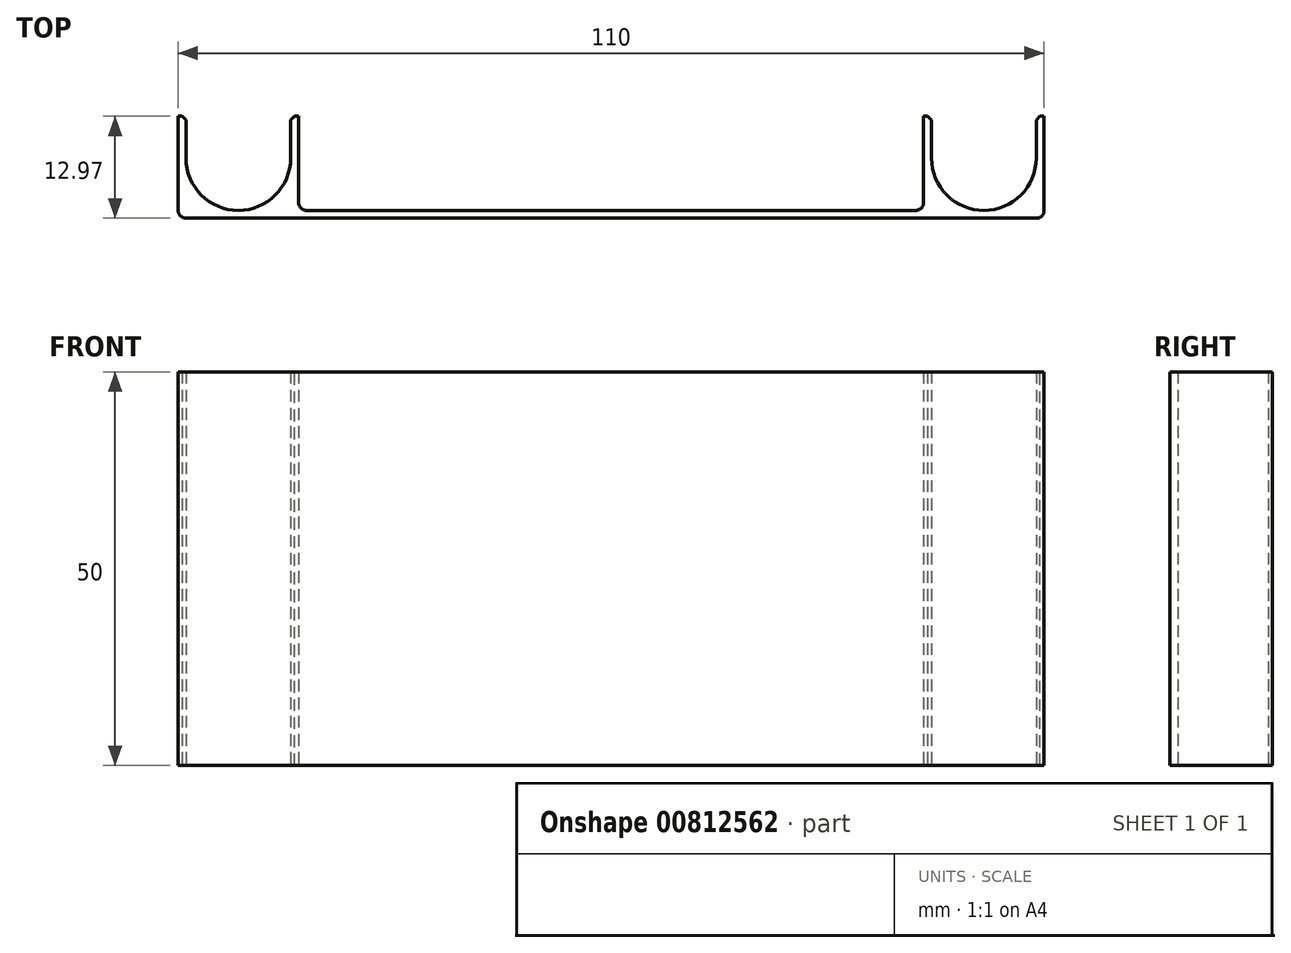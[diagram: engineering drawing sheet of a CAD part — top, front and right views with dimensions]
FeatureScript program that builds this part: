
annotation { "Feature Type Name" : "Feature", "Feature Type Description" : "" }
export const myFeature = defineFeature(function(context is Context, id is Id, definition is map)
    precondition{}
    {
        {
            assignVariable(context, id + "F0", {"name" : "length", "anyValue" : 50});
        }
        {
            var Q0;
            Q0=qCreatedBy(makeId("Top.planeOp"),FACE);
            var sketch = newSketch(context, id + "F1", { "sketchPlane" : qUnion([Q0])});
            skPoint(sketch, "E0.middle", {"position": v(0, 0) * mm});
            skLineSegment(sketch, "E1", {"start": v(-39.7, 1) * mm, "end": v(0, 1) * mm});
            skLineSegment(sketch, "E2", {"start": v(-55, 0) * mm, "end": v(0, 0) * mm});
            skLineSegment(sketch, "E3", {"start": v(0, 1) * mm, "end": v(0, 0) * mm, "construction": true});
            skLineSegment(sketch, "E4.MirrorCS", {"start": v(39.7, 1) * mm, "end": v(0, 1) * mm});
            skLineSegment(sketch, "E5.MirrorCS", {"start": v(55, 0) * mm, "end": v(0, 0) * mm});
            skLineSegment(sketch, "E6", {"start": v(-55, 0) * mm, "end": v(-55, 12.97) * mm});
            skLineSegment(sketch, "E7", {"start": v(-55, 12.97) * mm, "end": v(-54, 12.97) * mm});
            skLineSegment(sketch, "E8", {"start": v(-54, 12.97) * mm, "end": v(-54, 7.65) * mm});
            skLineSegment(sketch, "E9", {"start": v(-40.7, 7.65) * mm, "end": v(-40.7, 12.97) * mm});
            skLineSegment(sketch, "E10", {"start": v(-40.7, 12.97) * mm, "end": v(-39.7, 12.97) * mm});
            skLineSegment(sketch, "E11", {"start": v(-39.7, 12.97) * mm, "end": v(-39.7, 1) * mm});
            skLineSegment(sketch, "E12.MirrorCS", {"start": v(39.7, 12.97) * mm, "end": v(39.7, 1) * mm});
            skLineSegment(sketch, "E13.MirrorCS", {"start": v(40.7, 7.65) * mm, "end": v(40.7, 12.97) * mm});
            skLineSegment(sketch, "E14.MirrorCS", {"start": v(54, 12.97) * mm, "end": v(54, 7.65) * mm});
            skLineSegment(sketch, "E15.MirrorCS", {"start": v(55, 0) * mm, "end": v(55, 12.97) * mm});
            skLineSegment(sketch, "E16.MirrorCS", {"start": v(40.7, 12.97) * mm, "end": v(39.7, 12.97) * mm});
            skLineSegment(sketch, "E17.MirrorCS", {"start": v(55, 12.97) * mm, "end": v(54, 12.97) * mm});
            skArc(sketch, "E18", {"start": v(-54, 7.65) * mm, "mid": v(-47.35, 1) * mm, "end": v(-40.7, 7.65) * mm});
            skArc(sketch, "E19.MirrorCS", {"start": v(54, 7.65) * mm, "mid": v(47.35, 1) * mm, "end": v(40.7, 7.65) * mm});
            skSolve(sketch);
        }
        {
            var Q0;
            Q0 = qSketchRegion(id + "F1", true);
            extrude(context, id + "F2", {"entities" : qUnion([Q0]), "depth" : (getVariable(context, 'length')) * mm, "offsetDistance" : 25 * mm});
        }
        {
            var Q0;
            Q0=makeQuery(id+"F2.opExtrude","SWEPT_EDGE",EDGE,{"disambiguationData":[OSD([sQuery(id+"F1.wireOp",EDGE,"E2"),sQuery(id+"F1.wireOp",EDGE,"E6")])]});
            var Q1;
            Q1=makeQuery(id+"F2.opExtrude","SWEPT_EDGE",EDGE,{"disambiguationData":[OSD([sQuery(id+"F1.wireOp",EDGE,"E5.MirrorCS"),sQuery(id+"F1.wireOp",EDGE,"E15.MirrorCS")])]});
            var Q2;
            Q2=makeQuery(id+"F2.opExtrude","SWEPT_EDGE",EDGE,{"disambiguationData":[OSD([sQuery(id+"F1.wireOp",EDGE,"E4.MirrorCS"),sQuery(id+"F1.wireOp",EDGE,"E12.MirrorCS")])]});
            var Q3;
            Q3=makeQuery(id+"F2.opExtrude","SWEPT_EDGE",EDGE,{"disambiguationData":[OSD([sQuery(id+"F1.wireOp",EDGE,"E1"),sQuery(id+"F1.wireOp",EDGE,"E11")])]});
            fillet(context, id + "F3", {"entities" : qUnion([Q0, Q1, Q2, Q3]), "radius" : 1 * mm, "tangentPropagation" : true, "allowEdgeOverflow" : false});
        }
        {
            var Q0;
            Q0=makeQuery(id+"F2.opExtrude","SWEPT_EDGE",EDGE,{"disambiguationData":[OSD([sQuery(id+"F1.wireOp",EDGE,"E7"),sQuery(id+"F1.wireOp",EDGE,"E8")])]});
            var Q1;
            Q1=makeQuery(id+"F2.opExtrude","SWEPT_EDGE",EDGE,{"disambiguationData":[OSD([sQuery(id+"F1.wireOp",EDGE,"E9"),sQuery(id+"F1.wireOp",EDGE,"E10")])]});
            var Q2;
            Q2=makeQuery(id+"F2.opExtrude","SWEPT_EDGE",EDGE,{"disambiguationData":[OSD([sQuery(id+"F1.wireOp",EDGE,"E13.MirrorCS"),sQuery(id+"F1.wireOp",EDGE,"E16.MirrorCS")])]});
            var Q3;
            Q3=makeQuery(id+"F2.opExtrude","SWEPT_EDGE",EDGE,{"disambiguationData":[OSD([sQuery(id+"F1.wireOp",EDGE,"E14.MirrorCS"),sQuery(id+"F1.wireOp",EDGE,"E17.MirrorCS")])]});
            chamfer(context, id + "F4", {"entities" : qUnion([Q0, Q1, Q2, Q3]), "width" : .5 * mm, "tangentPropagation" : true});
        }
    });
